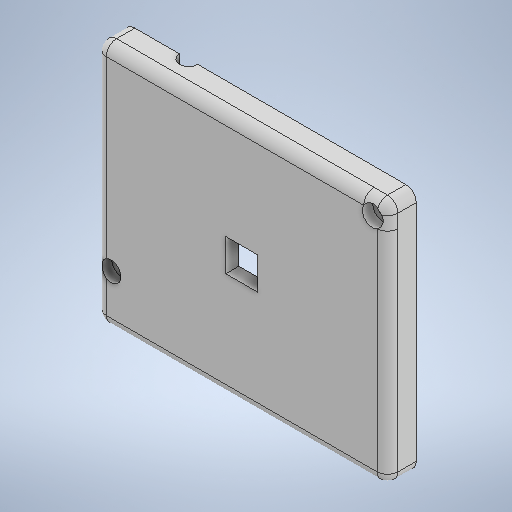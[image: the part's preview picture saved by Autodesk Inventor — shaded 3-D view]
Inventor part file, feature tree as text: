
AUTODESK INVENTOR PART (.ipt)
format: ipt  version: 2025.2 (Build 292293000, 293)  size: 345,088 bytes
history: native  units: mm
features: extrude x6, sketch x6, other x4, reference x3, projected_geometry x3, plane x1, fillet x1
ambient origin geometry x8: Origin, YZ Plane, XZ Plane, XY Plane, X Axis, Y Axis, Z Axis, Center Point
bodies: Volumenkörper1 (feature_tree)
feature tree (24):
  plane  "Arbeitsebene1"
  extrude  "Extrusion1"  Depth=2.5mm
  extrude  "Extrusion2"  Depth=2.0mm TaperAngle=0.0deg
  fillet  "Rundung1"  Radius=1.99mm
  extrude  "Extrusion3"  Depth=6.2mm
  extrude  "Extrusion4"  Depth=2.0mm
  extrude  "Extrusion5"  Depth=2.0mm
  extrude  "Extrusion6"  Depth=3.0mm TaperAngle=0.0deg
  sketch  "Skizze1"  dims[d0=2.5mm d1=0.0mm d2=3.8mm]
  reference  "Referenz1"
  sketch  "Skizze2"  dims[d3=3.8mm d4=2.0mm d5=0.0mm d6=1.99mm]
  reference  "Referenz2"
  reference  "Referenz3"
  sketch  "Skizze3"  dims[d7=6.1mm d8=6.2mm]
  sketch  "Skizze5"  dims[d9=0.0mm d10=0.0mm d11=2.0mm]
  projected_geometry  "Projizierte Kontur1"
  sketch  "Skizze6"  dims[d12=2.0mm d13=2.0mm]
  sketch  "Skizze7"  dims[d14=2.0mm d15=3.0mm d16=0.0mm d17=3.5mm d18=3.0mm d19=0.0mm d20=1.5mm d21=1.5mm d22=3.0mm d23=0.0mm]
  projected_geometry  "Projizierte Kontur2"
  projected_geometry  "Projizierte Kontur3"
  other  "<userpath>\OneDrive\Dokumente\Inventor\Programmierübung3\Baugruppe1.iam"
  other  "Baugruppe1.iam"
  other  "Case:1"
  other  "Baugruppe1"
